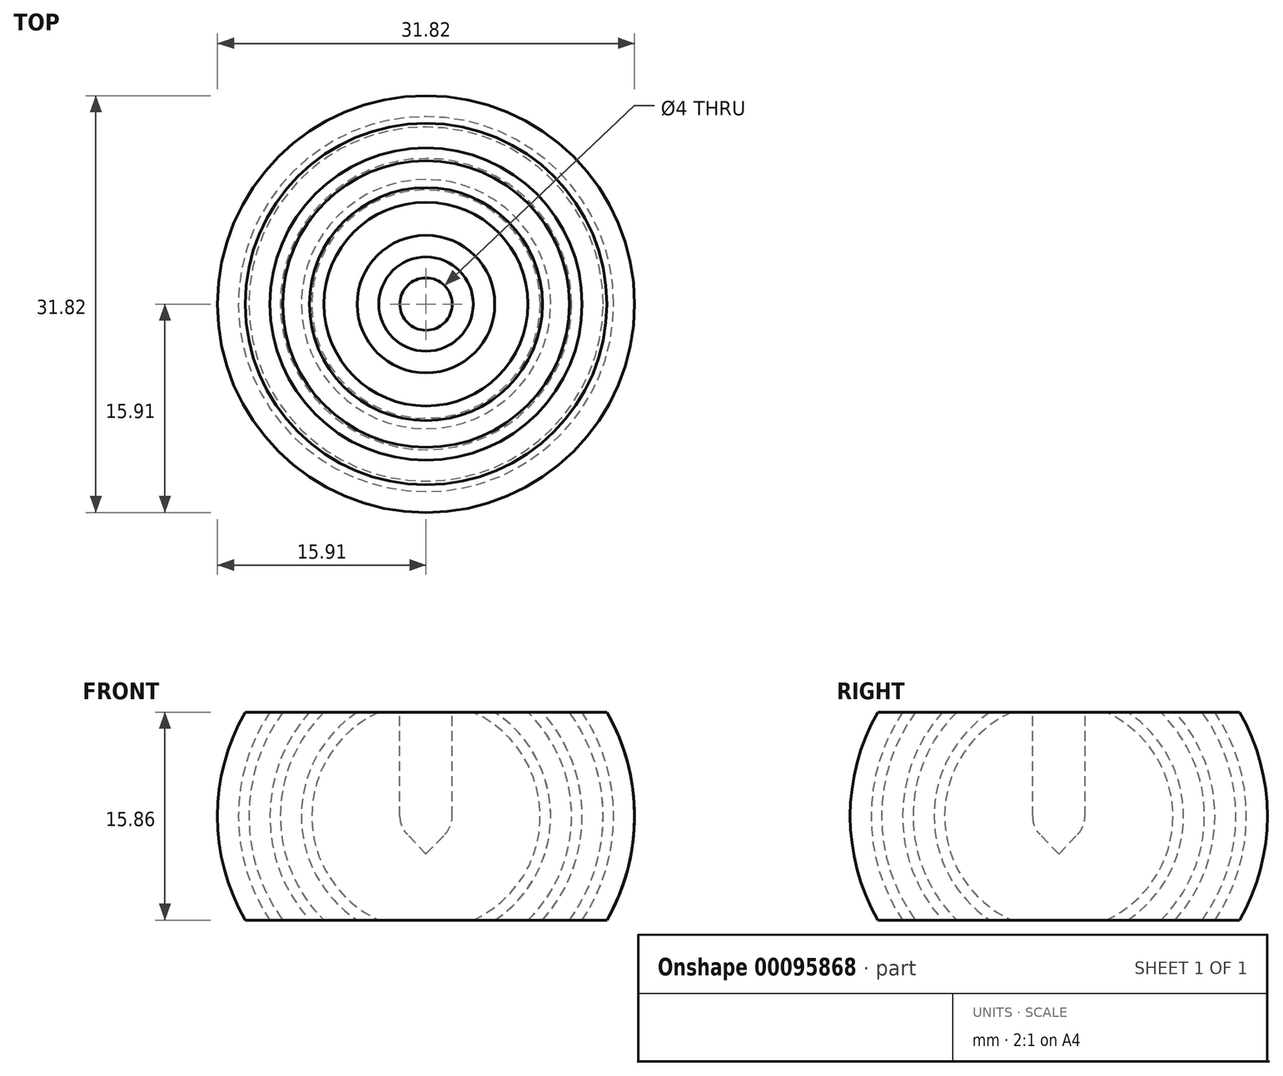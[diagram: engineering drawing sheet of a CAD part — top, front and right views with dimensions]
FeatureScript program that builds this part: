
annotation { "Feature Type Name" : "Feature", "Feature Type Description" : "" }
export const myFeature = defineFeature(function(context is Context, id is Id, definition is map)
    precondition{}
    {
        {
            var Q0;
            Q0=qCreatedBy(makeId("Front.planeOp"),FACE);
            var sketch = newSketch(context, id + "F0", { "sketchPlane" : qUnion([Q0])});
            skCircle(sketch, "E0", {"center": v(0, 0) * mm, "radius": 8.71 * mm});
            skCircle(sketch, "E1", {"center": v(0, 0) * mm, "radius": 9.51 * mm});
            skCircle(sketch, "E2", {"center": v(0, 0) * mm, "radius": 11.11 * mm});
            skCircle(sketch, "E3", {"center": v(0, 0) * mm, "radius": 11.91 * mm});
            skCircle(sketch, "E4", {"center": v(0, 0) * mm, "radius": 13.51 * mm});
            skCircle(sketch, "E5", {"center": v(0, 0) * mm, "radius": 14.31 * mm});
            skCircle(sketch, "E6", {"center": v(0, 0) * mm, "radius": 15.91 * mm});
            skPoint(sketch, "E7", {"position": v(-14.31, 0) * mm});
            skPoint(sketch, "E8", {"position": v(-11.91, 0) * mm});
            skPoint(sketch, "E9", {"position": v(-9.51, 0) * mm});
            skPoint(sketch, "E10", {"position": v(-15.91, 0) * mm});
            skPoint(sketch, "E11", {"position": v(-13.51, 0) * mm});
            skPoint(sketch, "E12", {"position": v(-11.11, 0) * mm});
            skPoint(sketch, "E13", {"position": v(-8.71, 0) * mm});
            skLineSegment(sketch, "E14", {"start": v(0, 7.93) * mm, "end": v(-32.85, 7.93) * mm});
            skPoint(sketch, "E15", {"position": v(-5.25, 7.93) * mm});
            skPoint(sketch, "E16", {"position": v(-8.89, 7.93) * mm});
            skPoint(sketch, "E17", {"position": v(-11.91, 7.93) * mm});
            skPoint(sketch, "E18", {"position": v(-3.6, 7.93) * mm});
            skLineSegment(sketch, "E19", {"start": v(0, 30.27) * mm, "end": v(0, -32.82) * mm});
            skLineSegment(sketch, "E20.MirrorCS", {"start": v(0, -7.93) * mm, "end": v(-32.85, -7.93) * mm});
            skLineSegment(sketch, "E21", {"start": v(-2, 7.93) * mm, "end": v(-2, -7.93) * mm});
            skCircle(sketch, "E22", {"center": v(0, 0) * mm, "radius": 2 * mm});
            skLineSegment(sketch, "E23", {"start": v(0, 2.88) * mm, "end": v(-1.44, 1.39) * mm});
            skLineSegment(sketch, "E24.MirrorCS", {"start": v(0, 2.88) * mm, "end": v(1.44, 1.39) * mm});
            skLineSegment(sketch, "E25.MirrorCS", {"start": v(0, -2.88) * mm, "end": v(-1.44, -1.39) * mm});
            skLineSegment(sketch, "E26.MirrorCS", {"start": v(0, -2.88) * mm, "end": v(1.44, -1.39) * mm});
            skSolve(sketch);
        }
        {
            var Q0;
            {var subQ1=sQuery(id+"F0.wireOp",EDGE,"E14");var subQ6=sQuery(id+"F0.wireOp",EDGE,"E0");var subQ8=makeQuery(id+"F0.imprint","INTERSECT",VERTEX,{"derivedFrom":[subQ6,subQ1]});Q0=makeQuery(id+"F0.imprint","IMPRINT",FACE,{"disambiguationData":[TD([[makeQuery(id+"F0.imprint","IMPRINT",EDGE,{"disambiguationData":[TD([[subQ8,-1.0]])],"derivedFrom":subQ6}),1.0]])]});}
            var Q1;
            {var subQ7=sQuery(id+"F0.wireOp",EDGE,"E25.MirrorCS");Q1=makeQuery(id+"F0.imprint","IMPRINT",FACE,{"disambiguationData":[TD([[makeQuery(id+"F0.imprint","IMPRINT",EDGE,{"derivedFrom":subQ7}),1.0]])]});}
            var Q2;
            {var subQ0=sQuery(id+"F0.wireOp",EDGE,"E14");var subQ1=sQuery(id+"F0.wireOp",EDGE,"E1");var subQ2=makeQuery(id+"F0.imprint","INTERSECT",VERTEX,{"derivedFrom":[subQ1,subQ0]});Q2=makeQuery(id+"F0.imprint","IMPRINT",FACE,{"disambiguationData":[TD([[makeQuery(id+"F0.imprint","IMPRINT",EDGE,{"disambiguationData":[TD([[subQ2,-1.0]])],"derivedFrom":subQ1}),-1.0]])]});}
            var Q3;
            {var subQ0=sQuery(id+"F0.wireOp",EDGE,"E14");var subQ1=sQuery(id+"F0.wireOp",EDGE,"E3");var subQ2=makeQuery(id+"F0.imprint","INTERSECT",VERTEX,{"derivedFrom":[subQ1,subQ0]});Q3=makeQuery(id+"F0.imprint","IMPRINT",FACE,{"disambiguationData":[TD([[makeQuery(id+"F0.imprint","IMPRINT",EDGE,{"disambiguationData":[TD([[subQ2,-1.0]])],"derivedFrom":subQ1}),-1.0]])]});}
            var Q4;
            {var subQ0=sQuery(id+"F0.wireOp",EDGE,"E14");var subQ1=sQuery(id+"F0.wireOp",EDGE,"E5");var subQ2=makeQuery(id+"F0.imprint","INTERSECT",VERTEX,{"derivedFrom":[subQ1,subQ0]});Q4=makeQuery(id+"F0.imprint","IMPRINT",FACE,{"disambiguationData":[TD([[makeQuery(id+"F0.imprint","IMPRINT",EDGE,{"disambiguationData":[TD([[subQ2,-1.0]])],"derivedFrom":subQ1}),-1.0]])]});}
            var Q5;
            Q5=sQuery(id+"F0.wireOp",EDGE,"E19");
            revolve(context, id + "F1", {"entities" : qUnion([Q0, Q1, Q2, Q3, Q4]), "axis" : qUnion([Q5]), "revolveType" : RevolveType.FULL});
        }
    });
